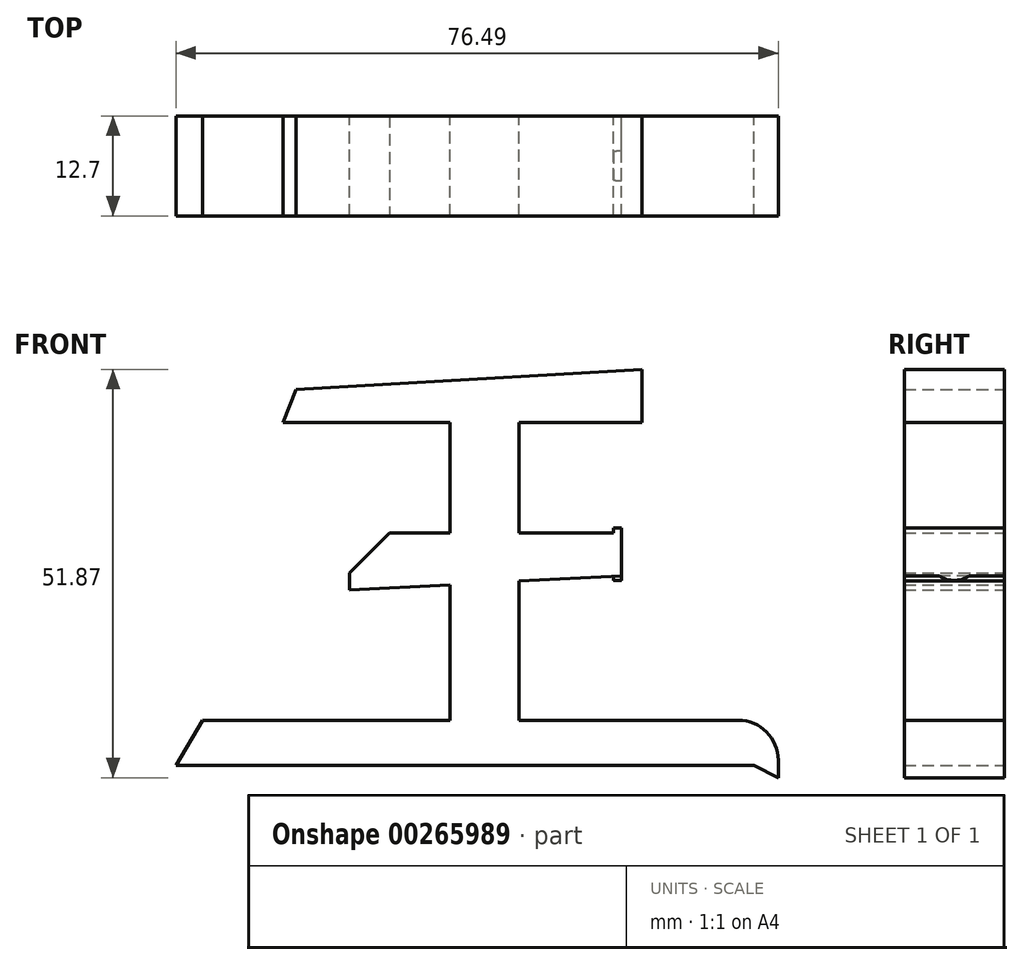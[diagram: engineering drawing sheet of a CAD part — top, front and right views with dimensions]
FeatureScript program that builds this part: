
annotation { "Feature Type Name" : "Feature", "Feature Type Description" : "" }
export const myFeature = defineFeature(function(context is Context, id is Id, definition is map)
    precondition{}
    {
        {
            var Q0;
            Q0=qCreatedBy(makeId("Front.planeOp"),FACE);
            var sketch = newSketch(context, id + "F0", { "sketchPlane" : qUnion([Q0])});
            skLineSegment(sketch, "E0", {"start": v(-25.45, 38.76) * mm, "end": v(18.47, 41.3) * mm});
            skLineSegment(sketch, "E1", {"start": v(18.47, 41.3) * mm, "end": v(18.47, 34.54) * mm});
            skLineSegment(sketch, "E2", {"start": v(18.47, 34.54) * mm, "end": v(-25.45, 34.54) * mm});
            skLineSegment(sketch, "E3", {"start": v(-5.9, 34.54) * mm, "end": v(-5.9, -3.27) * mm});
            skLineSegment(sketch, "E4", {"start": v(-5.9, -3.27) * mm, "end": v(-37.33, -3.27) * mm});
            skLineSegment(sketch, "E5", {"start": v(-40.7, -9) * mm, "end": v(32.7, -9) * mm});
            skLineSegment(sketch, "E6", {"start": v(35.8, -10.56) * mm, "end": v(35.8, -3.27) * mm});
            skLineSegment(sketch, "E7", {"start": v(35.8, -3.27) * mm, "end": v(2.86, -3.27) * mm});
            skLineSegment(sketch, "E8", {"start": v(2.86, -3.27) * mm, "end": v(2.86, 34.54) * mm});
            skLineSegment(sketch, "E9", {"start": v(-18.65, 20.55) * mm, "end": v(-18.65, 13.26) * mm});
            skLineSegment(sketch, "E10", {"start": v(-18.65, 13.26) * mm, "end": v(15.88, 15.1) * mm});
            skLineSegment(sketch, "E11", {"start": v(15.88, 15.1) * mm, "end": v(15.88, 20.55) * mm});
            skLineSegment(sketch, "E12", {"start": v(15.88, 20.55) * mm, "end": v(-18.65, 20.55) * mm});
            skLineSegment(sketch, "E13", {"start": v(-37.33, -3.27) * mm, "end": v(-40.7, -9) * mm});
            skLineSegment(sketch, "E14", {"start": v(-25.45, 38.76) * mm, "end": v(-27.09, 34.54) * mm});
            skLineSegment(sketch, "E15", {"start": v(-27.09, 34.54) * mm, "end": v(-25.45, 34.54) * mm});
            skLineSegment(sketch, "E16", {"start": v(32.7, -9) * mm, "end": v(35.8, -10.56) * mm});
            skLineSegment(sketch, "E17", {"start": v(15.88, 17.82) * mm, "end": v(2.86, 17.82) * mm});
            skLineSegment(sketch, "E18", {"start": v(15.88, 20.55) * mm, "end": v(15.88, 21.14) * mm});
            skLineSegment(sketch, "E19", {"start": v(15.88, 21.14) * mm, "end": v(14.89, 21.14) * mm});
            skLineSegment(sketch, "E20", {"start": v(14.89, 21.14) * mm, "end": v(14.89, 20.55) * mm});
            skSolve(sketch);
        }
        {
            var Q0;
            Q0 = qSketchRegion(id + "F0", true);
            extrude(context, id + "F1", {"entities" : qUnion([Q0]), "endBound" : BoundingType.SYMMETRIC, "depth" : 12.7 * mm});
        }
        {
            var Q0;
            Q0=makeQuery(id+"F1.opExtrude","SWEPT_EDGE",EDGE,{"disambiguationData":[OSD([sQuery(id+"F0.wireOp",EDGE,"E6"),sQuery(id+"F0.wireOp",EDGE,"E7")])]});
            fillet(context, id + "F2", {"entities" : qUnion([Q0]), "radius" : 5.08 * mm, "tangentPropagation" : true, "allowEdgeOverflow" : false});
        }
        {
            var Q0;
            {var subQ0=sQuery(id+"F0.wireOp",EDGE,"E18");Q0=makeQuery(id+"F0.imprint","IMPRINT",FACE,{"disambiguationData":[TD([[makeQuery(id+"F0.imprint","IMPRINT",EDGE,{"derivedFrom":subQ0}),1.0]])]});}
            var Q1;
            Q1=sQuery(id+"F0.wireOp",EDGE,"E17");
            revolve(context, id + "F3", {"operationType" : NewBodyOperationType.ADD, "entities" : qUnion([Q0]), "axis" : qUnion([Q1]), "revolveType" : RevolveType.FULL});
        }
        {
            var Q0;
            Q0=makeQuery(id+"F1.opExtrude","SWEPT_EDGE",EDGE,{"disambiguationData":[OSD([sQuery(id+"F0.wireOp",EDGE,"E9"),sQuery(id+"F0.wireOp",EDGE,"E12")])]});
            chamfer(context, id + "F4", {"entities" : qUnion([Q0]), "width" : 5.08 * mm, "tangentPropagation" : true});
        }
    });
